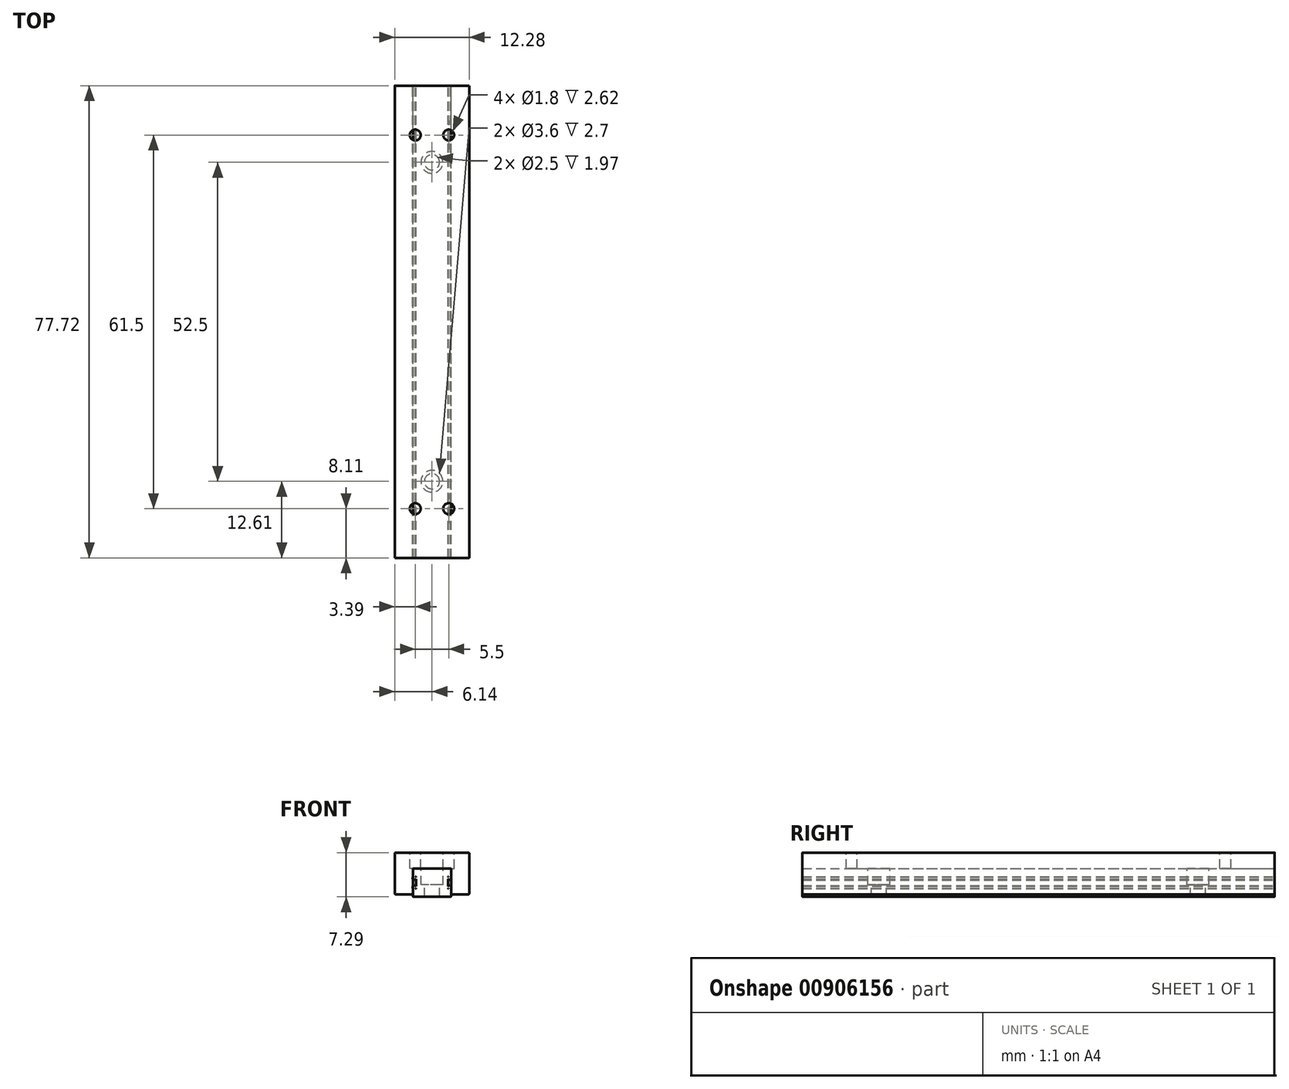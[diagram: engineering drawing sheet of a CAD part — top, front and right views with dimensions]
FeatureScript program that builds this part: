
annotation { "Feature Type Name" : "Feature", "Feature Type Description" : "" }
export const myFeature = defineFeature(function(context is Context, id is Id, definition is map)
    precondition{}
    {
        {
            var Q0;
            Q0=qCreatedBy(makeId("Front.planeOp"),FACE);
            var sketch = newSketch(context, id + "F0", { "sketchPlane" : qUnion([Q0])});
            skLineSegment(sketch, "E0", {"start": v(-3.14, 0) * mm, "end": v(3.14, 0) * mm});
            skLineSegment(sketch, "E1", {"start": v(3.14, 0) * mm, "end": v(3.14, 1.33) * mm});
            skLineSegment(sketch, "E2", {"start": v(3.14, 1.33) * mm, "end": v(3.06, 1.33) * mm});
            skLineSegment(sketch, "E3", {"start": v(2.64, 1.33) * mm, "end": v(2.64, 3.33) * mm});
            skLineSegment(sketch, "E4", {"start": v(2.64, 3.33) * mm, "end": v(2.72, 3.33) * mm});
            skLineSegment(sketch, "E5", {"start": v(3.14, 3.33) * mm, "end": v(3.14, 4.67) * mm});
            skLineSegment(sketch, "E6", {"start": v(3.14, 4.67) * mm, "end": v(-3.14, 4.67) * mm});
            skLineSegment(sketch, "E7", {"start": v(-3.14, 4.67) * mm, "end": v(-3.14, 3.33) * mm});
            skLineSegment(sketch, "E8", {"start": v(-3.14, 3.33) * mm, "end": v(-3.06, 3.33) * mm});
            skLineSegment(sketch, "E9", {"start": v(-2.64, 3.33) * mm, "end": v(-2.64, 3.25) * mm});
            skLineSegment(sketch, "E10", {"start": v(-2.64, 1.33) * mm, "end": v(-2.72, 1.33) * mm});
            skLineSegment(sketch, "E11", {"start": v(-3.14, 1.33) * mm, "end": v(-3.14, 0) * mm});
            skArc(sketch, "E12", {"start": v(2.64, 2.92) * mm, "mid": v(3.1, 2.87) * mm, "end": v(3.06, 3.33) * mm});
            skArc(sketch, "E13", {"start": v(2.64, 1.42) * mm, "mid": v(2.68, 1.37) * mm, "end": v(2.72, 1.33) * mm});
            skArc(sketch, "E14", {"start": v(-2.64, 3.25) * mm, "mid": v(-2.68, 3.3) * mm, "end": v(-2.72, 3.33) * mm});
            skArc(sketch, "E15", {"start": v(-2.64, 1.75) * mm, "mid": v(-3.1, 1.8) * mm, "end": v(-3.06, 1.33) * mm});
            skLineSegment(sketch, "E16.trimOffspring", {"start": v(-2.64, 2.92) * mm, "end": v(-2.64, 1.75) * mm});
            skArc(sketch, "E17.trimOffspring", {"start": v(-3.06, 3.33) * mm, "mid": v(-3.1, 2.87) * mm, "end": v(-2.64, 2.92) * mm});
            skLineSegment(sketch, "E18.trimOffspring", {"start": v(-3.06, 1.33) * mm, "end": v(-3.14, 1.33) * mm});
            skLineSegment(sketch, "E19.trimOffspring", {"start": v(-2.64, 1.42) * mm, "end": v(-2.64, 1.33) * mm});
            skArc(sketch, "E20.trimOffspring", {"start": v(-2.72, 1.33) * mm, "mid": v(-2.68, 1.37) * mm, "end": v(-2.64, 1.42) * mm});
            skLineSegment(sketch, "E21.trimOffspring", {"start": v(-2.72, 3.33) * mm, "end": v(-2.64, 3.33) * mm});
            skArc(sketch, "E22.trimOffspring", {"start": v(3.06, 1.33) * mm, "mid": v(3.1, 1.8) * mm, "end": v(2.64, 1.75) * mm});
            skLineSegment(sketch, "E23.trimOffspring", {"start": v(2.72, 1.33) * mm, "end": v(2.64, 1.33) * mm});
            skArc(sketch, "E24.trimOffspring", {"start": v(2.72, 3.33) * mm, "mid": v(2.68, 3.3) * mm, "end": v(2.64, 3.25) * mm});
            skLineSegment(sketch, "E25.trimOffspring", {"start": v(3.06, 3.33) * mm, "end": v(3.14, 3.33) * mm});
            skSolve(sketch);
        }
        {
            var Q0;
            Q0=makeQuery(id+"F0.imprint","IMPRINT",FACE,{"disambiguationData":[TD([[makeQuery(id+"F0.imprint","IMPRINT",EDGE,{"derivedFrom":sQuery(id+"F0.wireOp",EDGE,"E0")}),1.0]])]});
            extrude(context, id + "F1", {"entities" : qUnion([Q0]), "depth" : 77.72 * mm, "offsetDistance" : 25 * mm});
        }
        {
            var Q0;
            Q0=makeQuery(id+"F1.opExtrude","SWEPT_EDGE",EDGE,{"disambiguationData":[OSD([sQuery(id+"F0.wireOp",EDGE,"E6"),sQuery(id+"F0.wireOp",EDGE,"E7")])]});
            var Q1;
            Q1=makeQuery(id+"F1.opExtrude","SWEPT_EDGE",EDGE,{"disambiguationData":[OSD([sQuery(id+"F0.wireOp",EDGE,"E0"),sQuery(id+"F0.wireOp",EDGE,"E11")])]});
            var Q2;
            Q2=makeQuery(id+"F1.opExtrude","SWEPT_FACE",FACE,{"disambiguationData":[OSD([sQuery(id+"F0.wireOp",EDGE,"E0")])]});
            var Q3;
            Q3=makeQuery(id+"F1.opExtrude","SWEPT_EDGE",EDGE,{"disambiguationData":[OSD([sQuery(id+"F0.wireOp",EDGE,"E5"),sQuery(id+"F0.wireOp",EDGE,"E6")])]});
            fillet(context, id + "F2", {"entities" : qUnion([Q0, Q1, Q2, Q3]), "radius" : 0.1 * mm, "tangentPropagation" : true, "allowEdgeOverflow" : false});
        }
        {
            var Q0;
            Q0=makeQuery(id+"F1.opExtrude","SWEPT_FACE",FACE,{"disambiguationData":[OSD([sQuery(id+"F0.wireOp",EDGE,"E6")])]});
            var sketch = newSketch(context, id + "F3", { "sketchPlane" : qUnion([Q0])});
            skCircle(sketch, "E26", {"center": v(0, -65.11) * mm, "radius": 1.8 * mm});
            skCircle(sketch, "E27", {"center": v(0, -12.6) * mm, "radius": 1.8 * mm});
            skLineSegment(sketch, "E28", {"start": v(-3.04, -38.86) * mm, "end": v(3.04, -38.86) * mm, "construction": true});
            skSolve(sketch);
        }
        {
            var Q0;
            Q0 = qSketchRegion(id + "F3", true);
            extrude(context, id + "F4", {"entities" : qUnion([Q0]), "operationType" : NewBodyOperationType.REMOVE, "oppositeDirection" : true, "depth" : 2.7 * mm, "offsetDistance" : 25 * mm});
        }
        {
            var Q0;
            Q0=makeQuery(id+"F4.boolean.opBoolean","COPY",FACE,{"derivedFrom":makeQuery(id+"F4.opExtrude","CAP_FACE",FACE,{"disambiguationData":[OSD([sQuery(id+"F3.wireOp",EDGE,"E26")])],"isStart":false})});
            var sketch = newSketch(context, id + "F5", { "sketchPlane" : qUnion([Q0])});
            skCircle(sketch, "E29", {"center": v(0, -65.11) * mm, "radius": 1.25 * mm});
            skCircle(sketch, "E30", {"center": v(0, -12.6) * mm, "radius": 1.25 * mm});
            skSolve(sketch);
        }
        {
            var Q0;
            Q0 = qSketchRegion(id + "F5", true);
            extrude(context, id + "F6", {"entities" : qUnion([Q0]), "operationType" : NewBodyOperationType.REMOVE, "endBound" : BoundingType.UP_TO_NEXT, "oppositeDirection" : true, "depth" : 25 * mm, "offsetDistance" : 25 * mm});
        }
        {
            var Q0;
            Q0=makeQuery(id+"F1.opExtrude","CAP_FACE",FACE,{"disambiguationData":[OSD([sQuery(id+"F0.wireOp",EDGE,"E0"),sQuery(id+"F0.wireOp",EDGE,"E1"),sQuery(id+"F0.wireOp",EDGE,"E2"),sQuery(id+"F0.wireOp",EDGE,"E3"),sQuery(id+"F0.wireOp",EDGE,"E4"),sQuery(id+"F0.wireOp",EDGE,"E5"),sQuery(id+"F0.wireOp",EDGE,"E6"),sQuery(id+"F0.wireOp",EDGE,"E7"),sQuery(id+"F0.wireOp",EDGE,"E8"),sQuery(id+"F0.wireOp",EDGE,"E9"),sQuery(id+"F0.wireOp",EDGE,"E10"),sQuery(id+"F0.wireOp",EDGE,"E11"),sQuery(id+"F0.wireOp",EDGE,"E12"),sQuery(id+"F0.wireOp",EDGE,"E13"),sQuery(id+"F0.wireOp",EDGE,"E14"),sQuery(id+"F0.wireOp",EDGE,"E15"),sQuery(id+"F0.wireOp",EDGE,"E16.trimOffspring"),sQuery(id+"F0.wireOp",EDGE,"E17.trimOffspring"),sQuery(id+"F0.wireOp",EDGE,"E18.trimOffspring"),sQuery(id+"F0.wireOp",EDGE,"E19.trimOffspring"),sQuery(id+"F0.wireOp",EDGE,"E20.trimOffspring"),sQuery(id+"F0.wireOp",EDGE,"E21.trimOffspring"),sQuery(id+"F0.wireOp",EDGE,"E22.trimOffspring"),sQuery(id+"F0.wireOp",EDGE,"E23.trimOffspring"),sQuery(id+"F0.wireOp",EDGE,"E24.trimOffspring"),sQuery(id+"F0.wireOp",EDGE,"E25.trimOffspring")])],"isStart":true});
            var sketch = newSketch(context, id + "F7", { "sketchPlane" : qUnion([Q0])});
            skLineSegment(sketch, "E31", {"start": v(3.14, 0.4) * mm, "end": v(3.14, 4.67) * mm});
            skLineSegment(sketch, "E32", {"start": v(3.14, 4.67) * mm, "end": v(-3.14, 4.67) * mm});
            skLineSegment(sketch, "E33", {"start": v(-3.14, 4.67) * mm, "end": v(-3.14, 0.4) * mm});
            skLineSegment(sketch, "E34", {"start": v(-3.14, 0.4) * mm, "end": v(-6.14, 0.4) * mm});
            skLineSegment(sketch, "E35", {"start": v(-6.14, 0.4) * mm, "end": v(-6.14, 7.29) * mm});
            skLineSegment(sketch, "E36", {"start": v(-6.14, 7.29) * mm, "end": v(6.14, 7.3) * mm});
            skLineSegment(sketch, "E37", {"start": v(6.14, 7.3) * mm, "end": v(6.14, 0.4) * mm});
            skLineSegment(sketch, "E38", {"start": v(6.14, 0.4) * mm, "end": v(3.14, 0.4) * mm});
            skSolve(sketch);
        }
        {
            var Q0;
            Q0 = qSketchRegion(id + "F7", true);
            extrude(context, id + "F8", {"entities" : qUnion([Q0]), "oppositeDirection" : true, "depth" : 77.72 * mm, "offsetDistance" : 25 * mm});
        }
        {
            var Q0;
            Q0=makeQuery(id+"F8.opExtrude","SWEPT_EDGE",EDGE,{"disambiguationData":[OSD([sQuery(id+"F7.wireOp",EDGE,"E35"),sQuery(id+"F7.wireOp",EDGE,"E36")])]});
            var Q1;
            Q1=makeQuery(id+"F8.opExtrude","SWEPT_EDGE",EDGE,{"disambiguationData":[OSD([sQuery(id+"F7.wireOp",EDGE,"E36"),sQuery(id+"F7.wireOp",EDGE,"E37")])]});
            var Q2;
            Q2=makeQuery(id+"F8.opExtrude","SWEPT_EDGE",EDGE,{"disambiguationData":[OSD([sQuery(id+"F7.wireOp",EDGE,"E37"),sQuery(id+"F7.wireOp",EDGE,"E38")])]});
            var Q3;
            Q3=makeQuery(id+"F8.opExtrude","SWEPT_EDGE",EDGE,{"disambiguationData":[OSD([sQuery(id+"F7.wireOp",EDGE,"E34"),sQuery(id+"F7.wireOp",EDGE,"E35")])]});
            fillet(context, id + "F9", {"entities" : qUnion([Q0, Q1, Q2, Q3]), "radius" : 0.2 * mm, "tangentPropagation" : true, "allowEdgeOverflow" : false});
        }
        {
            var Q0;
            Q0=makeQuery(id+"F8.opExtrude","SWEPT_FACE",FACE,{"disambiguationData":[OSD([sQuery(id+"F7.wireOp",EDGE,"E36")])]});
            var sketch = newSketch(context, id + "F10", { "sketchPlane" : qUnion([Q0])});
            skCircle(sketch, "E39", {"center": v(-2.75, -8.1) * mm, "radius": 0.9 * mm});
            skCircle(sketch, "E40", {"center": v(2.75, -8.1) * mm, "radius": 0.9 * mm});
            skCircle(sketch, "E41", {"center": v(-2.75, -69.61) * mm, "radius": 0.9 * mm});
            skCircle(sketch, "E42", {"center": v(2.75, -69.61) * mm, "radius": 0.9 * mm});
            skLineSegment(sketch, "E43.bottom", {"start": v(-2.75, -69.61) * mm, "end": v(2.75, -69.61) * mm, "construction": true});
            skLineSegment(sketch, "E43.top", {"start": v(-2.75, -8.1) * mm, "end": v(2.75, -8.1) * mm, "construction": true});
            skLineSegment(sketch, "E43.left", {"start": v(-2.75, -69.61) * mm, "end": v(-2.75, -8.1) * mm, "construction": true});
            skLineSegment(sketch, "E43.right", {"start": v(2.75, -69.61) * mm, "end": v(2.75, -8.1) * mm, "construction": true});
            skPoint(sketch, "E43.middle", {"position": v(0, -38.86) * mm});
            skPoint(sketch, "E43.middle.positionSnap0", {"position": v(-5.94, -38.86) * mm});
            skPoint(sketch, "E43.centerSnap0", {"position": v(-5.94, -38.86) * mm});
            skSolve(sketch);
        }
        {
            var Q0;
            Q0 = qSketchRegion(id + "F10", true);
            var Q1;
            Q1=makeQuery(id+"F8.opExtrude","SWEPT_FACE",FACE,{"disambiguationData":[OSD([sQuery(id+"F7.wireOp",EDGE,"E32")])]});
            extrude(context, id + "F11", {"entities" : qUnion([Q0]), "operationType" : NewBodyOperationType.REMOVE, "endBound" : BoundingType.UP_TO_SURFACE, "oppositeDirection" : true, "depth" : 25 * mm, "endBoundEntityFace" : qUnion([Q1]), "offsetDistance" : 25 * mm});
        }
    });
